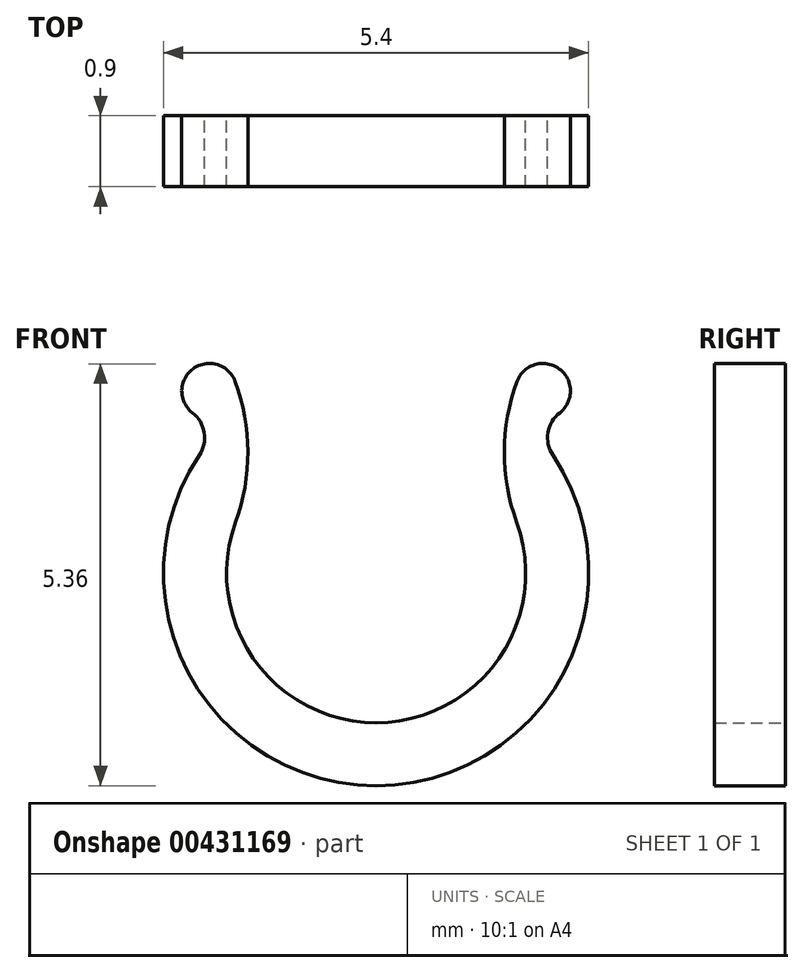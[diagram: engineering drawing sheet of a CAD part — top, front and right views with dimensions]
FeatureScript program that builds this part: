
annotation { "Feature Type Name" : "Feature", "Feature Type Description" : "" }
export const myFeature = defineFeature(function(context is Context, id is Id, definition is map)
    precondition{}
    {
        {
            var Q0;
            Q0=qCreatedBy(makeId("Front.planeOp"),FACE);
            var sketch = newSketch(context, id + "F0", { "sketchPlane" : qUnion([Q0])});
            skCircle(sketch, "E0", {"center": v(0, 0) * mm, "radius": 1.9 * mm, "construction": true});
            skCircle(sketch, "E1", {"center": v(0, 0) * mm, "radius": 2.7 * mm, "construction": true});
            skArc(sketch, "E2", {"start": v(-1.8, 2.44) * mm, "mid": v(-2.33, 2.6) * mm, "end": v(-2.33, 2.04) * mm});
            skArc(sketch, "E3", {"start": v(-2.25, 1.5) * mm, "mid": v(-2.18, 1.79) * mm, "end": v(-2.33, 2.04) * mm});
            skArc(sketch, "E4", {"start": v(-1.79, 0.65) * mm, "mid": v(-1.56, -1.09) * mm, "end": v(0, -1.9) * mm});
            skArc(sketch, "E5", {"start": v(-2.25, 1.5) * mm, "mid": v(-2.38, -1.27) * mm, "end": v(0, -2.7) * mm});
            skArc(sketch, "E6", {"start": v(-1.8, 2.44) * mm, "mid": v(-1.63, 1.54) * mm, "end": v(-1.79, 0.65) * mm});
            skLineSegment(sketch, "E7", {"start": v(0, 0) * mm, "end": v(0, -2.7) * mm, "construction": true});
            skLineSegment(sketch, "E8", {"start": v(0, 0) * mm, "end": v(-1.79, 0.65) * mm, "construction": true});
            skLineSegment(sketch, "E9", {"start": v(0, -1.9) * mm, "end": v(0, -2.7) * mm});
            skSolve(sketch);
        }
        {
            var Q0;
            Q0=makeQuery(id+"F0.imprint","IMPRINT",FACE,{"disambiguationData":[TD([[makeQuery(id+"F0.imprint","IMPRINT",EDGE,{"derivedFrom":sQuery(id+"F0.wireOp",EDGE,"E2")}),1.0]])]});
            extrude(context, id + "F1", {"entities" : qUnion([Q0]), "depth" : 0.9 * mm});
        }
        {
            var Q0;
            Q0=makeQuery(id+"F1.opExtrude","SWEPT_BODY",BODY,{"disambiguationData":[OSD([sQuery(id+"F0.wireOp",EDGE,"E2"),sQuery(id+"F0.wireOp",EDGE,"E3"),sQuery(id+"F0.wireOp",EDGE,"E4"),sQuery(id+"F0.wireOp",EDGE,"E5"),sQuery(id+"F0.wireOp",EDGE,"E6"),sQuery(id+"F0.wireOp",EDGE,"E9")])]});
            var Q1;
            Q1=qCreatedBy(makeId("Right.planeOp"),FACE);
            mirror(context, id + "F2", {"operationType" : NewBodyOperationType.ADD, "entities" : qUnion([Q0]), "mirrorPlane" : qUnion([Q1])});
        }
    });
